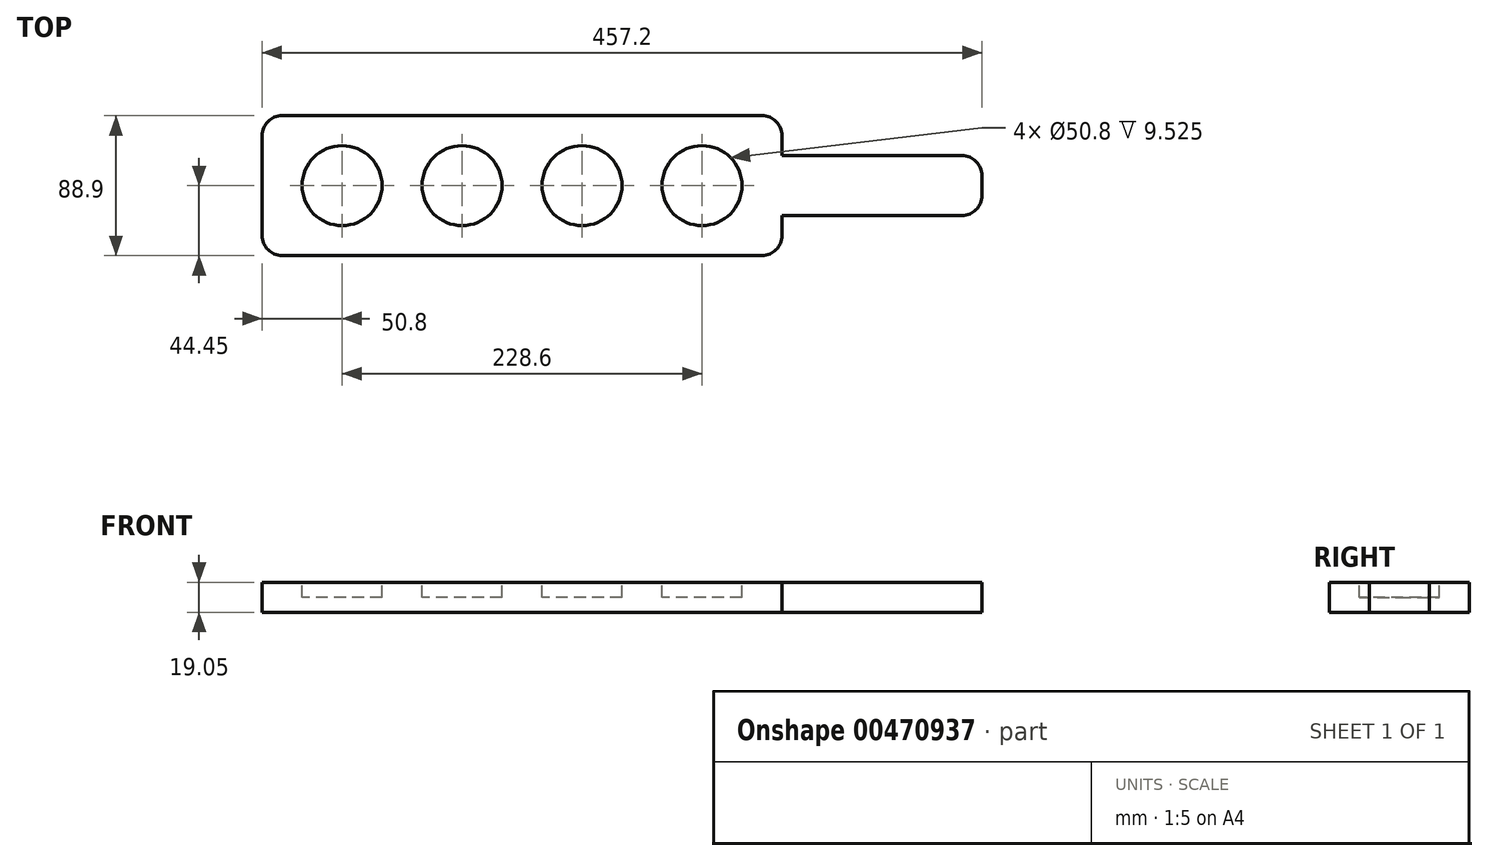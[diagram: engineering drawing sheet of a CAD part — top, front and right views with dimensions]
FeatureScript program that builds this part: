
annotation { "Feature Type Name" : "Feature", "Feature Type Description" : "" }
export const myFeature = defineFeature(function(context is Context, id is Id, definition is map)
    precondition{}
    {
        {
            var Q0;
            Q0=qCreatedBy(makeId("Top.planeOp"),FACE);
            var sketch = newSketch(context, id + "F0", { "sketchPlane" : qUnion([Q0])});
            skLineSegment(sketch, "E0.bottom", {"start": v(101.6, -44.45) * mm, "end": v(-228.6, -44.45) * mm});
            skLineSegment(sketch, "E0.top", {"start": v(101.6, 44.45) * mm, "end": v(-228.6, 44.45) * mm});
            skLineSegment(sketch, "E0.left", {"start": v(228.6, -19.05) * mm, "end": v(228.6, 19.05) * mm});
            skLineSegment(sketch, "E0.right", {"start": v(-228.6, -44.45) * mm, "end": v(-228.6, 44.45) * mm});
            skPoint(sketch, "E0.middle", {"position": v(0, 0) * mm});
            skLineSegment(sketch, "E1.top", {"start": v(228.6, 19.05) * mm, "end": v(101.6, 19.05) * mm});
            skLineSegment(sketch, "E1.right", {"start": v(101.6, 44.45) * mm, "end": v(101.6, 19.05) * mm});
            skLineSegment(sketch, "E2.top", {"start": v(228.6, -19.05) * mm, "end": v(101.6, -19.05) * mm});
            skLineSegment(sketch, "E2.right", {"start": v(101.6, -44.45) * mm, "end": v(101.6, -19.05) * mm});
            skLineSegment(sketch, "E3", {"start": v(0, 0) * mm, "end": v(228.6, 0) * mm, "construction": true});
            skSolve(sketch);
        }
        {
            var Q0;
            Q0 = qSketchRegion(id + "F0", true);
            extrude(context, id + "F1", {"entities" : qUnion([Q0]), "depth" : 19.05 * mm});
        }
        {
            var Q0;
            Q0=makeQuery(id+"F1.opExtrude","CAP_FACE",FACE,{"disambiguationData":[OSD([sQuery(id+"F0.wireOp",EDGE,"E0.bottom"),sQuery(id+"F0.wireOp",EDGE,"E0.top"),sQuery(id+"F0.wireOp",EDGE,"E0.left"),sQuery(id+"F0.wireOp",EDGE,"E0.right"),sQuery(id+"F0.wireOp",EDGE,"E1.top"),sQuery(id+"F0.wireOp",EDGE,"E1.right"),sQuery(id+"F0.wireOp",EDGE,"E2.top"),sQuery(id+"F0.wireOp",EDGE,"E2.right")])],"isStart":false});
            var sketch = newSketch(context, id + "F2", { "sketchPlane" : qUnion([Q0])});
            skCircle(sketch, "E4", {"center": v(-177.8, 0) * mm, "radius": 25.4 * mm});
            skLineSegment(sketch, "E5", {"start": v(-177.8, 0) * mm, "end": v(-203.2, 0) * mm, "construction": true});
            skLineSegment(sketch, "E6", {"start": v(-203.2, 0) * mm, "end": v(-228.6, 0) * mm, "construction": true});
            skCircle(sketch, "E7.1.0.0", {"center": v(-101.6, 0) * mm, "radius": 25.4 * mm});
            skCircle(sketch, "E7.2.0.0", {"center": v(-25.4, 0) * mm, "radius": 25.4 * mm});
            skCircle(sketch, "E7.3.0.0", {"center": v(50.8, 0) * mm, "radius": 25.4 * mm});
            skLineSegment(sketch, "E7.direction1", {"start": v(-177.8, 0) * mm, "end": v(-101.6, 0) * mm, "construction": true});
            skSolve(sketch);
        }
        {
            var Q0;
            Q0 = qSketchRegion(id + "F2", true);
            extrude(context, id + "F3", {"entities" : qUnion([Q0]), "operationType" : NewBodyOperationType.REMOVE, "oppositeDirection" : true, "depth" : 9.52 * mm});
        }
        {
            var Q0;
            Q0=makeQuery(id+"F1.opExtrude","SWEPT_EDGE",EDGE,{"disambiguationData":[OSD([sQuery(id+"F0.wireOp",EDGE,"E0.bottom"),sQuery(id+"F0.wireOp",EDGE,"E0.right")])]});
            var Q1;
            Q1=makeQuery(id+"F1.opExtrude","SWEPT_EDGE",EDGE,{"disambiguationData":[OSD([sQuery(id+"F0.wireOp",EDGE,"E0.bottom"),sQuery(id+"F0.wireOp",EDGE,"E2.right")])]});
            var Q2;
            Q2=makeQuery(id+"F1.opExtrude","SWEPT_EDGE",EDGE,{"disambiguationData":[OSD([sQuery(id+"F0.wireOp",EDGE,"E0.top"),sQuery(id+"F0.wireOp",EDGE,"E1.right")])]});
            var Q3;
            Q3=makeQuery(id+"F1.opExtrude","SWEPT_EDGE",EDGE,{"disambiguationData":[OSD([sQuery(id+"F0.wireOp",EDGE,"E0.left"),sQuery(id+"F0.wireOp",EDGE,"E2.top")])]});
            var Q4;
            Q4=makeQuery(id+"F1.opExtrude","SWEPT_EDGE",EDGE,{"disambiguationData":[OSD([sQuery(id+"F0.wireOp",EDGE,"E0.left"),sQuery(id+"F0.wireOp",EDGE,"E1.top")])]});
            var Q5;
            Q5=makeQuery(id+"F1.opExtrude","SWEPT_EDGE",EDGE,{"disambiguationData":[OSD([sQuery(id+"F0.wireOp",EDGE,"E0.top"),sQuery(id+"F0.wireOp",EDGE,"E0.right")])]});
            fillet(context, id + "F4", {"entities" : qUnion([Q0, Q1, Q2, Q3, Q4, Q5]), "radius" : 12.7 * mm, "tangentPropagation" : true, "allowEdgeOverflow" : false});
        }
    });
